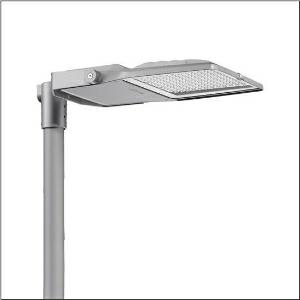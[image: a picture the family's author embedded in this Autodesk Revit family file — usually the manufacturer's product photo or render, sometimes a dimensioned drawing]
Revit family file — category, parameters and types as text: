
# Revit family: floodlight_fl_21_midi___pl61_5xa7785f2c3a_30c2
name_source: partatom
category: Lighting Fixtures
units: mm (PartAtom-declared; Revit-internal decimal feet)

## family parameters
Cut with Voids When Loaded = No
Host = Face
Light Source = No
Part Type = Normal
Room Calculation Point = No
Round Connector Dimension = Use Diameter
Shared = No

## types (1)
- --- (1 x LED, 35100 lm, 271.6 W, 3000K)
    Apparent Load = 272 VA
    CIE Flux Codes = 33 65 98 100 100
    Color Rendering = 70
    Color Temperature = 3000K
    Default Elevation = 1800 mm
    Description = Floodlight FL 21 midi, floodlight, primary light control with lens, of PMMA, primary optical cover: protective disc, of toughened safety glass, transparent, light distribution: PL61, light emission: direct distribution, installation type: surface-mounted, LED, High Power LED, rated luminous flux: 35.100lm, luminous efficacy: 129lm/W, light colour: 730, colour temperature: 3000K, control gear: Smart Interface (Zhaga), control: flexible luminous flux parameterisation, time-dependent luminous flux control, constant luminous flux control, overheat protection, pre-setting: logarithmic dimming characteristic, with terminal, 6-pole, mains connection: 220..240V, AC, 50/60Hz, start of lifetime: 272W, end of service life: 287W, reduction: 123W, luminaire housing, of diecast aluminium, powder-coated, SITECO metallic grey (DB 702S), corrosivity category C5 mid according to DIN EN ISO 12944, suitable for swimming pools, chlorine-resistant, sealing non-destructively replaceable, please order mast flange separately, mast bracket, of steel, galvanised, powder-coated, SITECO metallic grey (DB 702S), Smart Interface above, protection rating (complete): IP66, insulation class (complete): insulation class II (safety insulation), certification: CE, ENEC, VDE, protection symbol: D, impact resistance: IK08, permissible operating ambient temperature: -40..+40°C, permissible operating ambient temperature for outdoor applications: -40..+50°C, standard: DIN EN 12944, LABS conformity tested according to VDMA 24364:2018-05, packaging unit: 1 piece

Light Distribution: PL61
    Height = 76 mm
    Lamp = 1 x LED
    Lamp Light Flux = 35100 lm
    Lamp Power = 271.6 W
    Lamp count = 1
    Length = 657 mm
    Luminous efficacy = 129 lm/W
    Manufacturer = Siteco
    ModVariant = No
    Model = 5XA7785F2C3A
    Number of Poles = 1
    OnlyDefault = Yes
    Power Factor = 1
    Product Name = Floodlight FL 21 midi | PL61
    Product group = floodlight | pylon annexe
    ProductGroupID = 6201
    Protection Class = Protection class II
    Protection Degree = IP 66
    RLX_Detail_Level = 1
    RLX_Emergency_Light_Flux = 0 lm
    RLX_Emergency_Type = 0
    RLX_Emergency_Type_DB = No
    RlxData = <blob elided: 153709 chars, md5=4dbda6a7>
    Socket = socket
    Standby Power = 0 W
    System Light Flux = 35100 lm
    System Power = 272 W
    Type Comments = factory setting: luminous flux: 100 % | dim-lin: 254 | 620 mA
    Type Image = l_1007123.jpg
    URL = http://relux.com
    VarID = @adj_191465
    Voltage = 0 V
    Weight = 0.00 kg
    Width = 442 mm

## geometry (parser evidence)
native form markers: Blend x4, Sweep x14
no freeform markers — native parametric forms only
